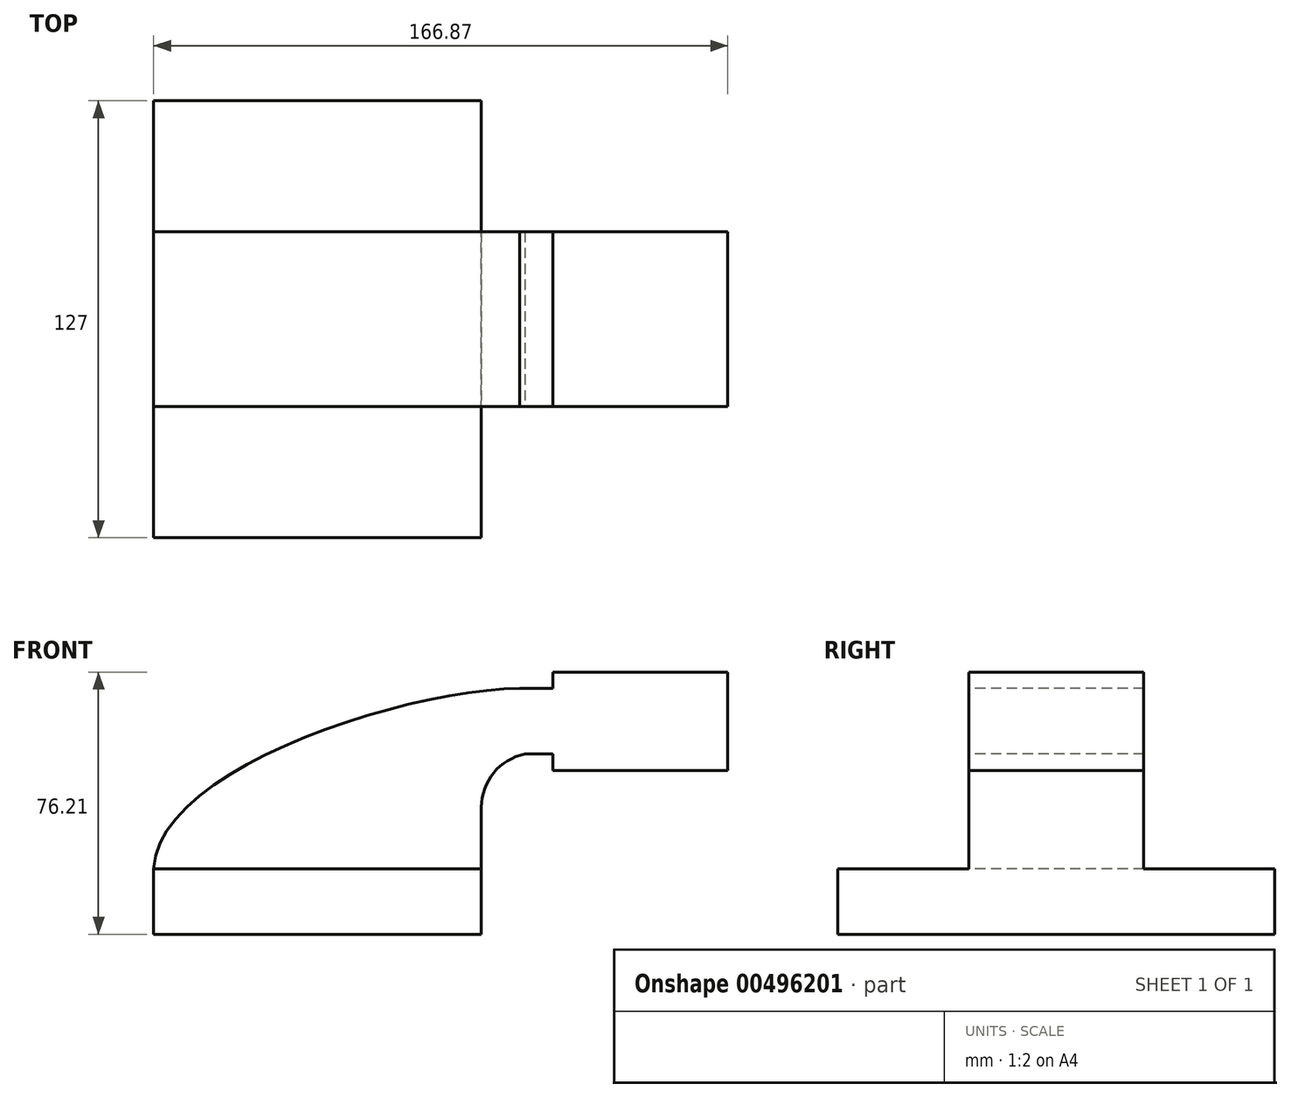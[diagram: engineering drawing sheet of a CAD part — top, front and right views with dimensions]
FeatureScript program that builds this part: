
annotation { "Feature Type Name" : "Feature", "Feature Type Description" : "" }
export const myFeature = defineFeature(function(context is Context, id is Id, definition is map)
    precondition{}
    {
        {
            var Q0;
            Q0=qCreatedBy(makeId("Front.planeOp"),FACE);
            var sketch = newSketch(context, id + "F0", { "sketchPlane" : qUnion([Q0])});
            skLineSegment(sketch, "E0.bottom", {"start": v(-47.62, -9.53) * mm, "end": v(47.63, -9.53) * mm});
            skLineSegment(sketch, "E0.top", {"start": v(-47.63, 9.52) * mm, "end": v(47.63, 9.52) * mm});
            skLineSegment(sketch, "E0.left", {"start": v(-47.63, -9.53) * mm, "end": v(-47.63, 9.52) * mm});
            skLineSegment(sketch, "E0.right", {"start": v(47.63, -9.53) * mm, "end": v(47.63, 9.52) * mm});
            skPoint(sketch, "E0.middle", {"position": v(0, 0) * mm});
            skLineSegment(sketch, "E1.bottom", {"start": v(119.24, 66.67) * mm, "end": v(68.44, 66.67) * mm});
            skLineSegment(sketch, "E1.top", {"start": v(119.24, 38.1) * mm, "end": v(68.44, 38.1) * mm});
            skLineSegment(sketch, "E1.left", {"start": v(119.24, 66.67) * mm, "end": v(119.24, 38.1) * mm});
            skLineSegment(sketch, "E1.right", {"start": v(68.44, 66.67) * mm, "end": v(68.44, 38.1) * mm});
            skPoint(sketch, "E1.middle", {"position": v(93.84, 52.39) * mm});
            skLineSegment(sketch, "E2", {"start": v(47.63, 9.52) * mm, "end": v(47.63, 27.32) * mm});
            skArc(sketch, "E3", {"start": v(47.62, 27.32) * mm, "mid": v(51.2, 37.36) * mm, "end": v(60.33, 42.88) * mm});
            skLineSegment(sketch, "E4", {"start": v(60.33, 42.88) * mm, "end": v(93.84, 42.88) * mm});
            skLineSegment(sketch, "E5.0", {"start": v(58.8, 61.93) * mm, "end": v(93.84, 61.93) * mm});
            skArc(sketch, "E5.1", {"start": v(28.58, 27.32) * mm, "mid": v(37.2, 50.3) * mm, "end": v(58.8, 61.93) * mm});
            skLineSegment(sketch, "E5.2", {"start": v(28.57, 9.52) * mm, "end": v(28.57, 27.32) * mm});
            skFitSpline(sketch, "E6", {"points": [v(-47.62, 9.52) * mm, v(58.8, 61.93) * mm], "startDerivative": vector(3.47, 86.74) * mm, "endDerivative": vector(101.48, 1.07) * mm});
            skSolve(sketch);
        }
        {
            var Q0;
            Q0=makeQuery(id+"F0.imprint","IMPRINT",FACE,{"disambiguationData":[TD([[makeQuery(id+"F0.imprint","IMPRINT",EDGE,{"derivedFrom":sQuery(id+"F0.wireOp",EDGE,"E0.bottom")}),1.0]])]});
            extrude(context, id + "F1", {"entities" : qUnion([Q0]), "endBound" : BoundingType.SYMMETRIC, "depth" : 127 * mm});
        }
        {
            var Q0;
            Q0 = qSketchRegion(id + "F0", true);
            extrude(context, id + "F2", {"entities" : qUnion([Q0]), "operationType" : NewBodyOperationType.ADD, "endBound" : BoundingType.SYMMETRIC, "oppositeDirection" : true, "depth" : 50.8 * mm});
        }
    });
